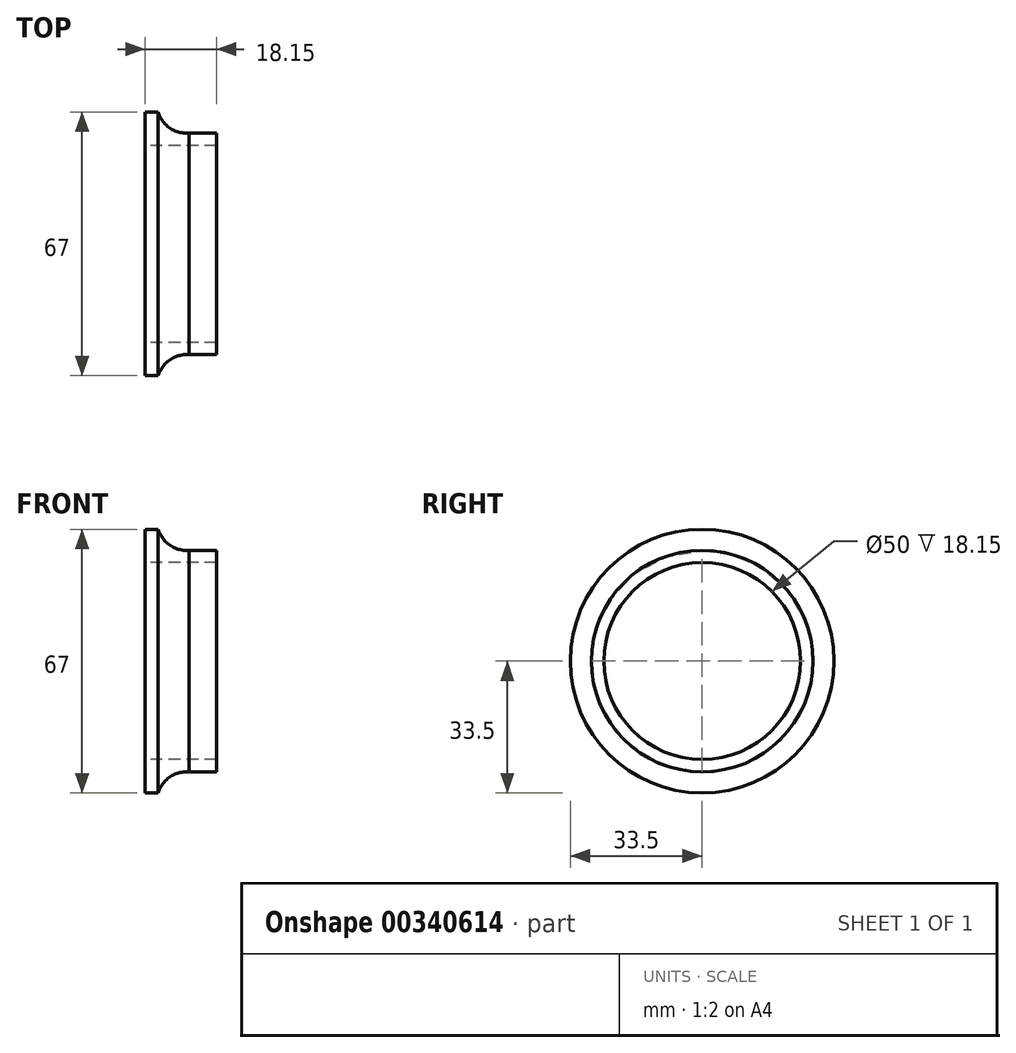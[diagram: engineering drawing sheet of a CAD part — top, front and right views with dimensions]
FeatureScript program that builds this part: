
annotation { "Feature Type Name" : "Feature", "Feature Type Description" : "" }
export const myFeature = defineFeature(function(context is Context, id is Id, definition is map)
    precondition{}
    {
        {
            var Q0;
            Q0=qCreatedBy(makeId("Front.planeOp"),FACE);
            var sketch = newSketch(context, id + "F0", { "sketchPlane" : qUnion([Q0])});
            skLineSegment(sketch, "E0", {"start": v(0, 33.5) * mm, "end": v(3.3, 33.5) * mm});
            skLineSegment(sketch, "E1", {"start": v(0, 25) * mm, "end": v(18.15, 25) * mm});
            skLineSegment(sketch, "E2", {"start": v(18.15, 25) * mm, "end": v(18.15, 28.15) * mm});
            skLineSegment(sketch, "E3", {"start": v(18.15, 28.15) * mm, "end": v(11.15, 28.15) * mm});
            skArc(sketch, "E4", {"start": v(3.3, 33.5) * mm, "mid": v(6.28, 29.45) * mm, "end": v(11.15, 28.15) * mm});
            skLineSegment(sketch, "E5", {"start": v(0, 25) * mm, "end": v(0, 33.5) * mm});
            skSolve(sketch);
        }
        {
            var Q0;
            Q0=qCreatedBy(makeId("Front.planeOp"),FACE);
            var sketch = newSketch(context, id + "F1", { "sketchPlane" : qUnion([Q0])});
            skLineSegment(sketch, "E6", {"start": v(0, 0) * mm, "end": v(20.54, 0) * mm});
            skSolve(sketch);
        }
        {
            var Q0;
            Q0=makeQuery(id+"F0.imprint","IMPRINT",FACE,{"disambiguationData":[TD([[makeQuery(id+"F0.imprint","IMPRINT",EDGE,{"derivedFrom":sQuery(id+"F0.wireOp",EDGE,"E0")}),-1.0]])]});
            var Q1;
            Q1=sQuery(id+"F1.wireOp",EDGE,"E6");
            revolve(context, id + "F2", {"entities" : qUnion([Q0]), "axis" : qUnion([Q1]), "revolveType" : RevolveType.FULL});
        }
    });
